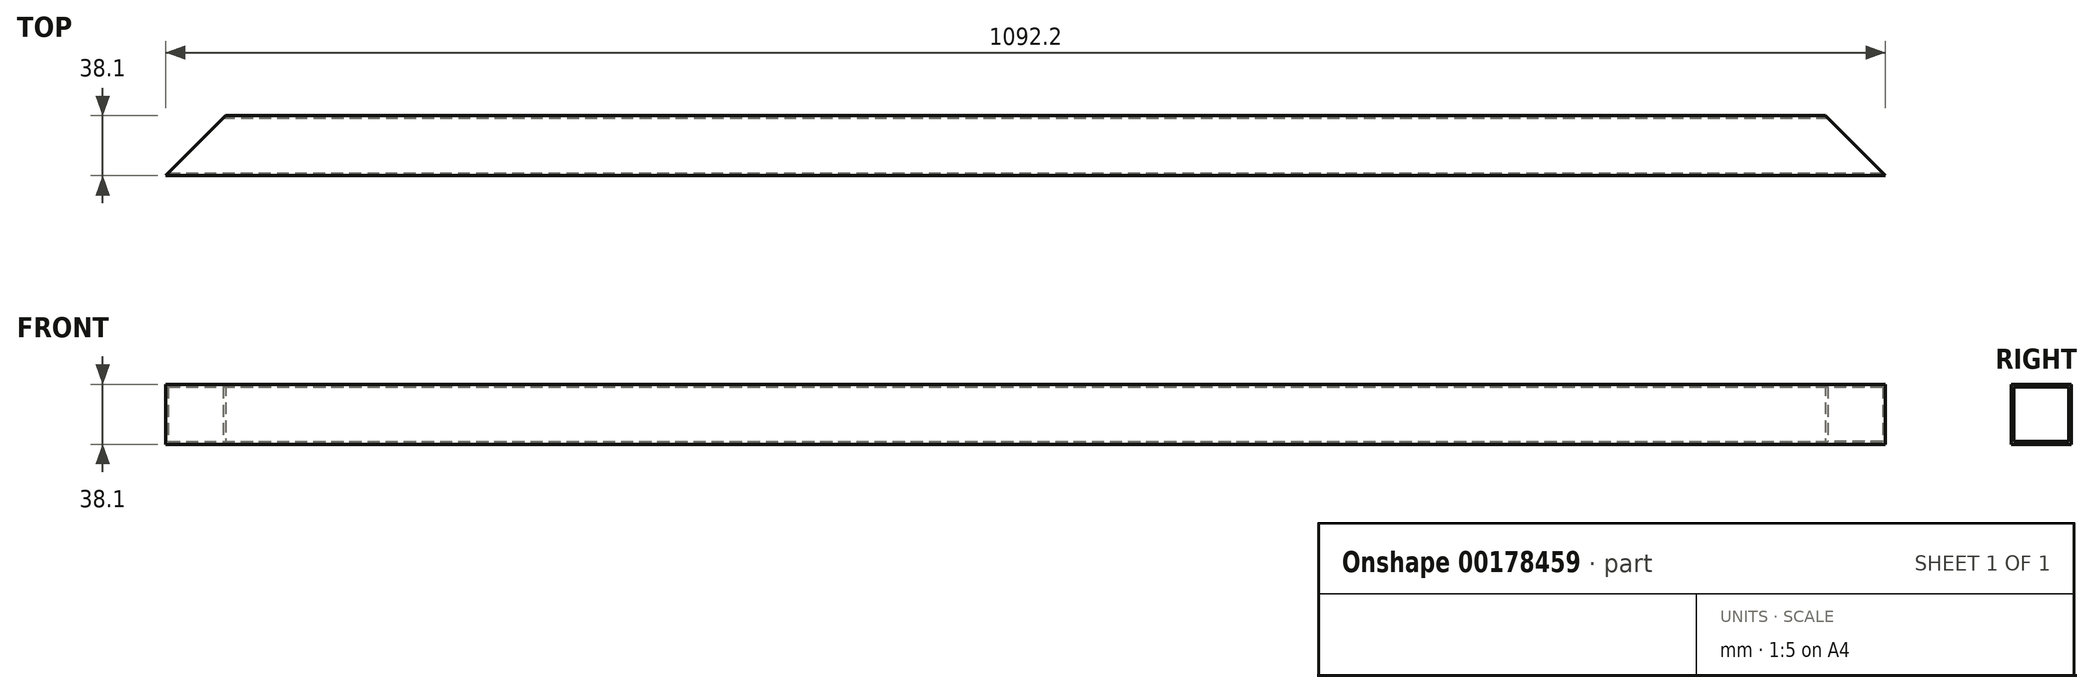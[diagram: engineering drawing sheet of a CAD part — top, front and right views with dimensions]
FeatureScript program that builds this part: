
annotation { "Feature Type Name" : "Feature", "Feature Type Description" : "" }
export const myFeature = defineFeature(function(context is Context, id is Id, definition is map)
    precondition{}
    {
        {
            var Q0;
            Q0=qCreatedBy(makeId("Top.planeOp"),FACE);
            var sketch = newSketch(context, id + "F0", { "sketchPlane" : qUnion([Q0])});
            skLineSegment(sketch, "E0", {"start": v(0, 0) * mm, "end": v(-508, 0) * mm});
            skLineSegment(sketch, "E1", {"start": v(-508, 0) * mm, "end": v(-546.1, -38.1) * mm});
            skLineSegment(sketch, "E2", {"start": v(-546.1, -38.1) * mm, "end": v(0, -38.1) * mm});
            skLineSegment(sketch, "E3.MirrorCS", {"start": v(0, 0) * mm, "end": v(508, 0) * mm});
            skLineSegment(sketch, "E4.MirrorCS", {"start": v(508, 0) * mm, "end": v(546.1, -38.1) * mm});
            skLineSegment(sketch, "E5.MirrorCS", {"start": v(546.1, -38.1) * mm, "end": v(0, -38.1) * mm});
            skSolve(sketch);
        }
        {
            var Q0;
            Q0=makeQuery(id+"F0.imprint","IMPRINT",FACE,{"disambiguationData":[TD([[makeQuery(id+"F0.imprint","IMPRINT",EDGE,{"derivedFrom":sQuery(id+"F0.wireOp",EDGE,"E0")}),1.0]])]});
            extrude(context, id + "F1", {"entities" : qUnion([Q0]), "depth" : 38.1 * mm});
        }
        {
            var Q0;
            Q0=qCreatedBy(makeId("Right.planeOp"),FACE);
            var sketch = newSketch(context, id + "F2", { "sketchPlane" : qUnion([Q0])});
            skLineSegment(sketch, "E6.bottom", {"start": v(-36.45, 36.45) * mm, "end": v(-1.65, 36.45) * mm});
            skLineSegment(sketch, "E6.top", {"start": v(-36.45, 1.65) * mm, "end": v(-1.65, 1.65) * mm});
            skLineSegment(sketch, "E6.left", {"start": v(-36.45, 36.45) * mm, "end": v(-36.45, 1.65) * mm});
            skLineSegment(sketch, "E6.right", {"start": v(-1.65, 36.45) * mm, "end": v(-1.65, 1.65) * mm});
            skPoint(sketch, "E6.middle", {"position": v(-19.05, 19.05) * mm});
            skSolve(sketch);
        }
        {
            var Q0;
            Q0 = qSketchRegion(id + "F2", true);
            extrude(context, id + "F3", {"entities" : qUnion([Q0]), "operationType" : NewBodyOperationType.REMOVE, "endBound" : BoundingType.THROUGH_ALL, "oppositeDirection" : true, "depth" : 25.4 * mm, "hasSecondDirection" : true, "secondDirectionBound" : SecondDirectionBoundingType.THROUGH_ALL, "secondDirectionOppositeDirection" : false, "secondDirectionDepth" : 25.4 * mm});
        }
    });
